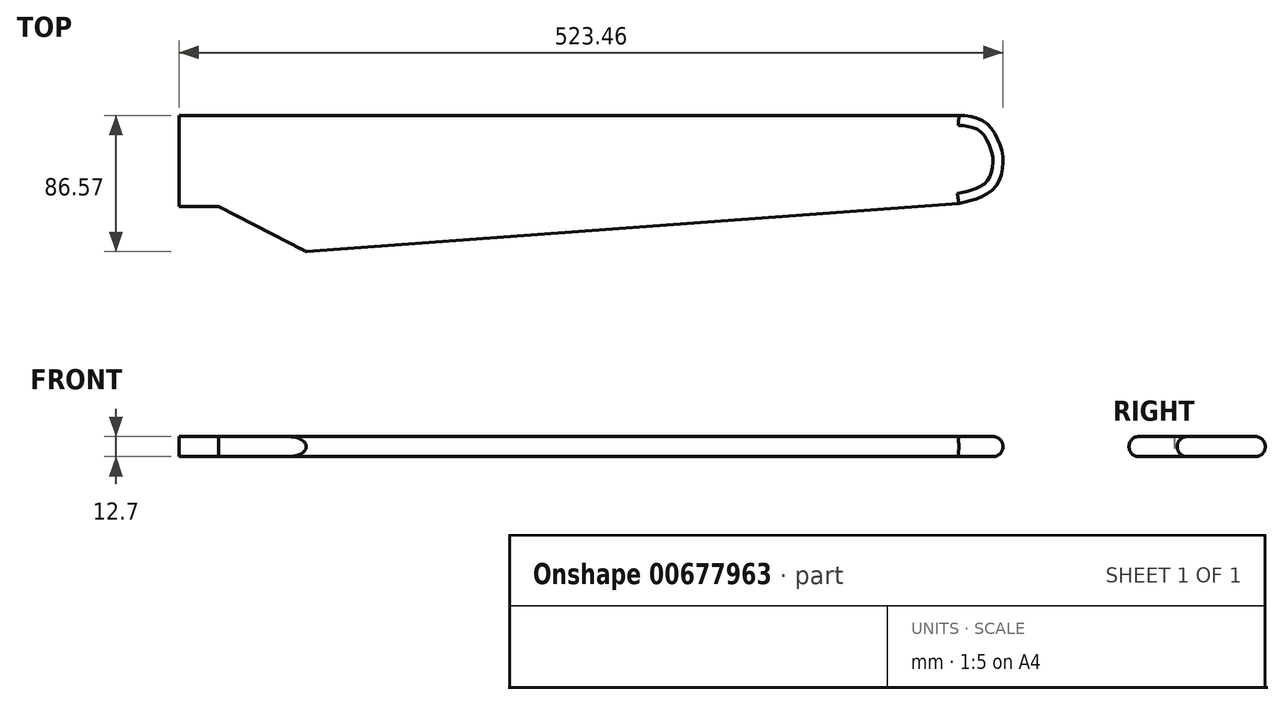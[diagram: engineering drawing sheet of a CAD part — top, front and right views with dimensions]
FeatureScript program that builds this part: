
annotation { "Feature Type Name" : "Feature", "Feature Type Description" : "" }
export const myFeature = defineFeature(function(context is Context, id is Id, definition is map)
    precondition{}
    {
        {
            var Q0;
            Q0=qCreatedBy(makeId("Top.planeOp"),FACE);
            var sketch = newSketch(context, id + "F0", { "sketchPlane" : qUnion([Q0])});
            skLineSegment(sketch, "E0.bottom", {"start": v(-66.09, 36.15) * mm, "end": v(-40.9, 36.15) * mm});
            skLineSegment(sketch, "E0.top", {"start": v(-66.09, -21.74) * mm, "end": v(-40.9, -21.74) * mm});
            skLineSegment(sketch, "E0.left", {"start": v(-66.09, 36.15) * mm, "end": v(-66.09, -21.74) * mm});
            skLineSegment(sketch, "E0.right", {"start": v(-40.9, 36.15) * mm, "end": v(-40.9, -21.74) * mm});
            skLineSegment(sketch, "E1", {"start": v(-40.9, 36.15) * mm, "end": v(429.24, 36.15) * mm});
            skFitSpline(sketch, "E2", {"points": [v(429.24, 36.15) * mm, v(453.42, 21.94) * mm, v(457.24, 9.83) * mm, v(452.37, -9.34) * mm, v(429.24, -19.85) * mm], "startDerivative": vector(185.02, -8.6) * mm, "endDerivative": vector(-103.26, -21.44) * mm});
            skLineSegment(sketch, "E3", {"start": v(429.24, -19.85) * mm, "end": v(14.9, -50.42) * mm});
            skLineSegment(sketch, "E4", {"start": v(14.9, -50.42) * mm, "end": v(-40.9, -21.74) * mm});
            skSolve(sketch);
        }
        {
            var Q0;
            Q0=makeQuery(id+"F0.imprint","IMPRINT",FACE,{"disambiguationData":[TD([[makeQuery(id+"F0.imprint","IMPRINT",EDGE,{"derivedFrom":sQuery(id+"F0.wireOp",EDGE,"E0.right")}),1.0]])]});
            var Q1;
            Q1=makeQuery(id+"F0.imprint","IMPRINT",FACE,{"disambiguationData":[TD([[makeQuery(id+"F0.imprint","IMPRINT",EDGE,{"derivedFrom":sQuery(id+"F0.wireOp",EDGE,"E0.bottom")}),-1.0]])]});
            extrude(context, id + "F1", {"entities" : qUnion([Q0, Q1]), "depth" : 12.7 * mm, "offsetDistance" : 25.4 * mm});
        }
        {
            var Q0;
            Q0=makeQuery(id+"F1.opExtrude","CAP_EDGE",EDGE,{"disambiguationData":[OSD([sQuery(id+"F0.wireOp",EDGE,"E3")])],"isStart":false});
            var Q1;
            Q1=makeQuery(id+"F1.opExtrude","CAP_EDGE",EDGE,{"disambiguationData":[OSD([sQuery(id+"F0.wireOp",EDGE,"E2")])],"isStart":false});
            var Q2;
            Q2=makeQuery(id+"F1.opExtrude","CAP_EDGE",EDGE,{"disambiguationData":[OSD([sQuery(id+"F0.wireOp",EDGE,"E0.bottom"),sQuery(id+"F0.wireOp",EDGE,"E1")])],"isStart":false});
            var Q3;
            Q3=makeQuery(id+"F1.opExtrude","CAP_EDGE",EDGE,{"disambiguationData":[OSD([sQuery(id+"F0.wireOp",EDGE,"E3")])],"isStart":true});
            var Q4;
            Q4=makeQuery(id+"F1.opExtrude","CAP_EDGE",EDGE,{"disambiguationData":[OSD([sQuery(id+"F0.wireOp",EDGE,"E2")])],"isStart":true});
            var Q5;
            Q5=makeQuery(id+"F1.opExtrude","CAP_EDGE",EDGE,{"disambiguationData":[OSD([sQuery(id+"F0.wireOp",EDGE,"E0.bottom"),sQuery(id+"F0.wireOp",EDGE,"E1")])],"isStart":true});
            fillet(context, id + "F2", {"entities" : qUnion([Q0, Q1, Q2, Q3, Q4, Q5]), "radius" : 6.35 * mm, "tangentPropagation" : true, "allowEdgeOverflow" : false});
        }
    });
